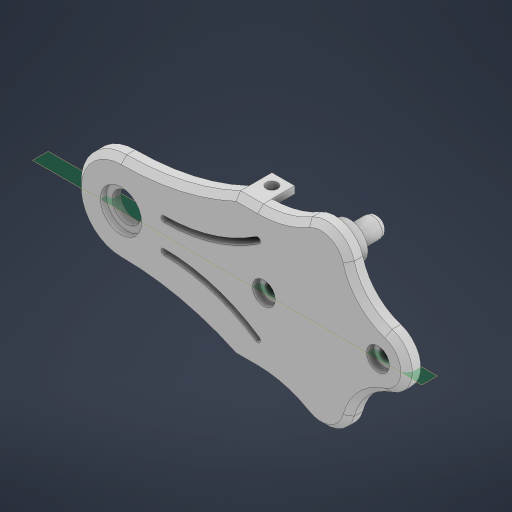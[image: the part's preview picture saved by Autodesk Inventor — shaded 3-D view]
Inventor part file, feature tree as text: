
AUTODESK INVENTOR PART (.ipt)
format: ipt  version: 2024.2 (Build 282272000, 272)  size: 455,168 bytes
history: native  units: in
note: dims shown in document units (in); Inventor stores cm internally (conversion verified against a paired STEP export)
features: extrude x12, sketch x10, projected_geometry x7, mirror x3, plane x1, fillet x1, chamfer x1
ambient origin geometry x8: Origin, YZ Plane, XZ Plane, XY Plane, X Axis, Y Axis, Z Axis, Center Point
bodies: Solid1 (feature_tree)
feature tree (35):
  extrude  "Extrusion1"  Depth=1.9685in
  plane  "Work Plane1"
  extrude  "Extrusion3"  Depth=0.1969in TaperAngle=0.0deg
  mirror  "Mirror1"
  extrude  "Extrusion4"  Depth=0.1575in
  extrude  "Extrusion5"  Depth=0.3677in
  mirror  "Mirror2"
  sketch  "Sketch7"  dims[d16=0.0787in d17=0.3937in]
  extrude  "Extrusion6"  Depth=0.3937in
  extrude  "Extrusion7"  Depth=0.5906in
  extrude  "Extrusion8"  TaperAngle=0.0deg  [1 undecoded]
  fillet  "Fillet1"  Radius=0.315in
  extrude  "Extrusion9"  Depth=0.315in TaperAngle=0.0deg
  mirror  "Mirror3"
  extrude  "Extrusion10"  Depth=0.1575in
  extrude  "Extrusion11"  Depth=0.3937in
  sketch  "Sketch12"  dims[d29=0.315in d30=0.0in d31=0.7874in d32=0.8268in d33=0.3937in d34=0.0in d35=0.5118in d36=0.1969in d37=0.0in d38=0.2756in d39=0.3937in d40=0.0in d41=0.0787in d42=0.0in d43=0.0in d44=0.6299in d45=0.315in d46=0.0984in d47=0.0in d48=0.5697in d49=0.0787in d50=0.0in d51=0.0787in d52=0.0787in d53=45.0deg d54=0.7874in d55=0.7874in d56=0.7874in d57=0.1575in d58=0.7874in d59=0.7874in d60=0.3937in d61=0.0in d62=0.3937in d63=0.0in]
  extrude  "Extrusion12"  Depth=0.3937in
  extrude  "Extrusion13"  Depth=0.3937in TaperAngle=0.0deg
  chamfer  "Chamfer1"  Distance=0.5118in
  sketch  "Sketch1"  dims[d1=0.4in d3=1.9685in]
  sketch  "Sketch4"  dims[d4=2.3441in d5=0.1969in d6=0.0in]
  sketch  "Sketch5"  dims[d12=0.1575in d13=1.5748in]
  projected_geometry  "Projected Loop1"
  sketch  "Sketch6"  dims[d14=1.971in d15=0.3677in]
  projected_geometry  "Projected Loop2"
  projected_geometry  "Projected Loop3"
  sketch  "Sketch8"  dims[d18=0.315in d19=0.5906in]
  projected_geometry  "Projected Loop4"
  sketch  "Sketch9"  dims[d20=0.1969in d21=0.0in d22=0.0in d23=0.315in]
  projected_geometry  "Projected Loop5"
  sketch  "Sketch10"  dims[d24=0.0984in d25=0.315in d26=0.0in]
  projected_geometry  "Projected Loop6"
  sketch  "Sketch11"  dims[d27=0.1575in d28=0.1575in]
  projected_geometry  "Projected Loop7"
note: 1 required parameter value undecoded (feature->parameter linkage not recoverable at this tier; creation-order binding heuristic only, values carry confidence <= 0.55)
